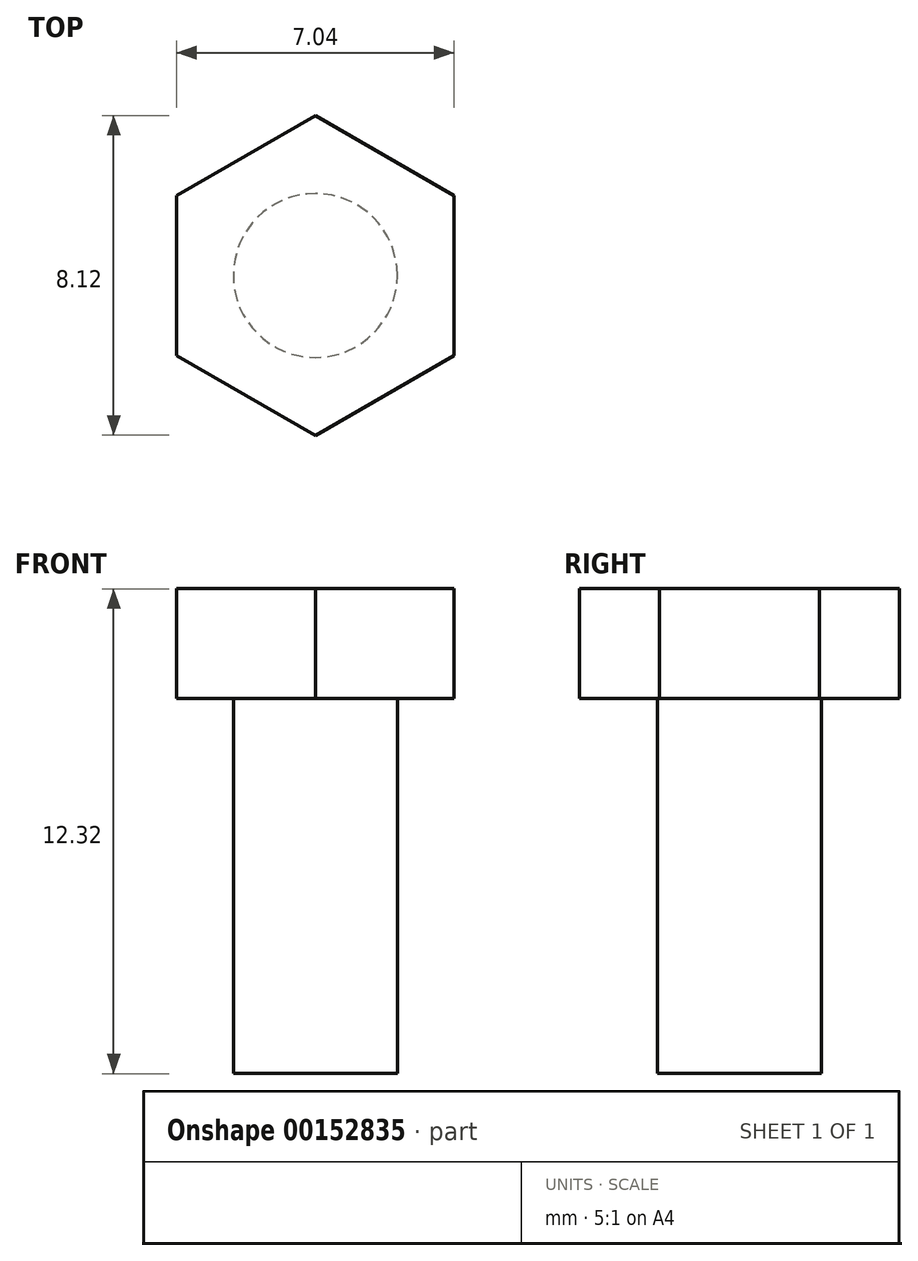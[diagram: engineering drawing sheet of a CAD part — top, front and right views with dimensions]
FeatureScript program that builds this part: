
annotation { "Feature Type Name" : "Feature", "Feature Type Description" : "" }
export const myFeature = defineFeature(function(context is Context, id is Id, definition is map)
    precondition{}
    {
        {
            var Q0;
            Q0=qCreatedBy(makeId("Top.planeOp"),FACE);
            var sketch = newSketch(context, id + "F0", { "sketchPlane" : qUnion([Q0])});
            skCircle(sketch, "E0.cCircle", {"center": v(0, 0) * mm, "radius": 4.06 * mm, "construction": true});
            skLineSegment(sketch, "E0.0", {"start": v(0, 4.06) * mm, "end": v(3.52, 2.03) * mm});
            skLineSegment(sketch, "E0.1", {"start": v(3.52, 2.03) * mm, "end": v(3.52, -2.03) * mm});
            skLineSegment(sketch, "E0.2", {"start": v(3.52, -2.03) * mm, "end": v(0, -4.06) * mm});
            skLineSegment(sketch, "E0.3", {"start": v(0, -4.06) * mm, "end": v(-3.52, -2.03) * mm});
            skLineSegment(sketch, "E0.4", {"start": v(-3.52, -2.03) * mm, "end": v(-3.52, 2.03) * mm});
            skLineSegment(sketch, "E0.5", {"start": v(-3.52, 2.03) * mm, "end": v(0, 4.06) * mm});
            skSolve(sketch);
        }
        {
            var Q0;
            Q0 = qSketchRegion(id + "F0", true);
            extrude(context, id + "F1", {"entities" : qUnion([Q0]), "depth" : 2.8 * mm});
        }
        {
            var Q0;
            Q0=makeQuery(id+"F1.opExtrude","CAP_FACE",FACE,{"disambiguationData":[OSD([sQuery(id+"F0.wireOp",EDGE,"E0.0"),sQuery(id+"F0.wireOp",EDGE,"E0.1"),sQuery(id+"F0.wireOp",EDGE,"E0.2"),sQuery(id+"F0.wireOp",EDGE,"E0.3"),sQuery(id+"F0.wireOp",EDGE,"E0.4"),sQuery(id+"F0.wireOp",EDGE,"E0.5")])],"isStart":true});
            var sketch = newSketch(context, id + "F2", { "sketchPlane" : qUnion([Q0])});
            skCircle(sketch, "E1", {"center": v(0, 0) * mm, "radius": 2.08 * mm});
            skSolve(sketch);
        }
        {
            var Q0;
            Q0 = qSketchRegion(id + "F2", true);
            extrude(context, id + "F3", {"entities" : qUnion([Q0]), "operationType" : NewBodyOperationType.ADD, "depth" : 9.52 * mm});
        }
    });
